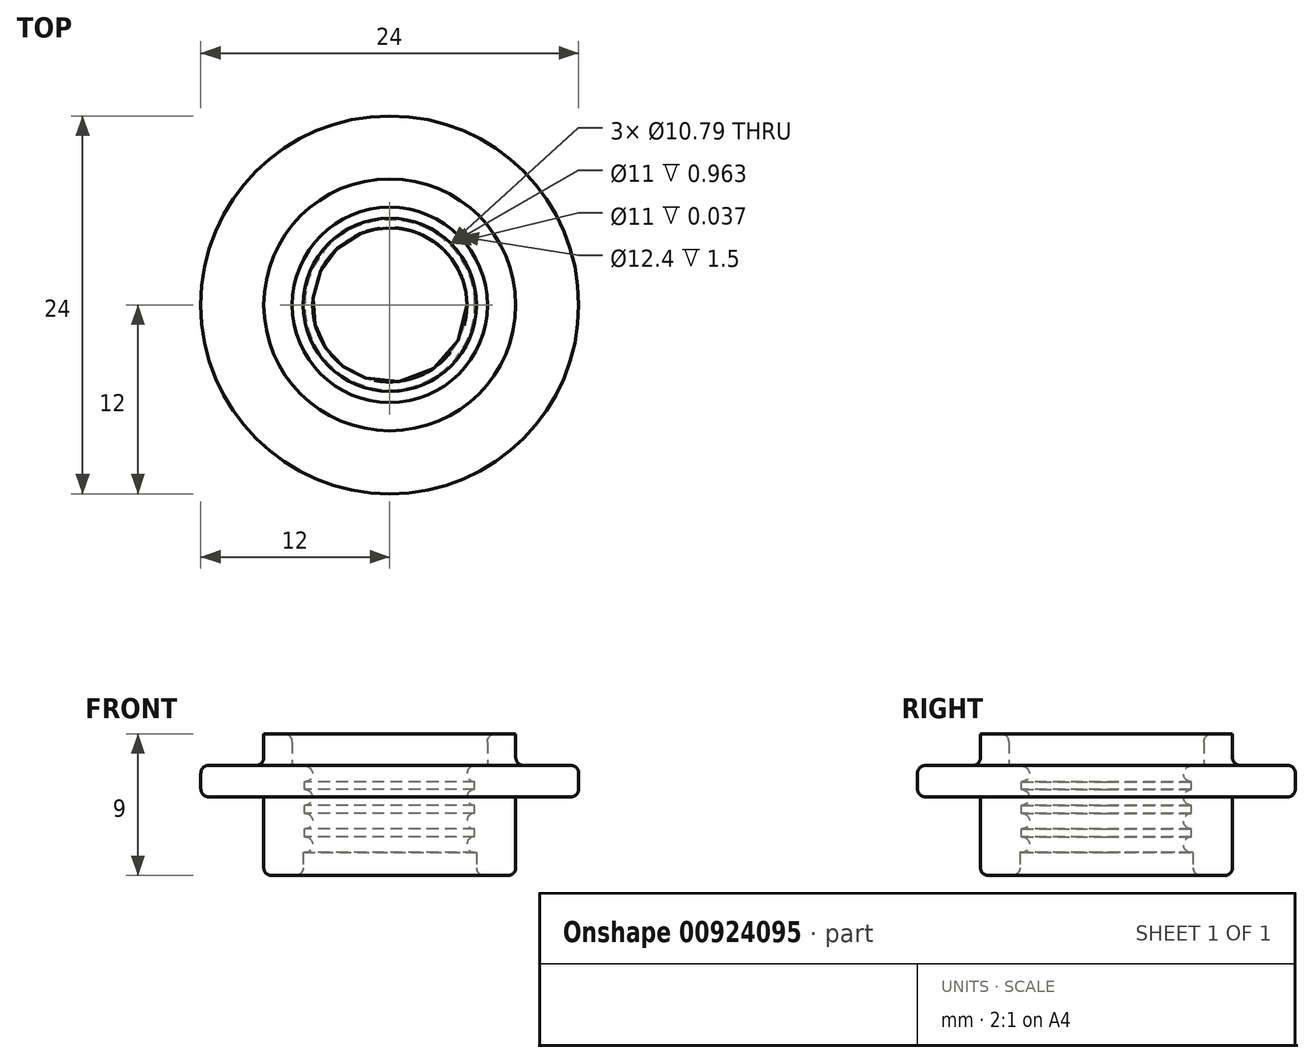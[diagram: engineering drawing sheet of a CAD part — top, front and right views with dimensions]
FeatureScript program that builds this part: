
annotation { "Feature Type Name" : "Feature", "Feature Type Description" : "" }
export const myFeature = defineFeature(function(context is Context, id is Id, definition is map)
    precondition{}
    {
        {
            var Q0;
            Q0=qCreatedBy(makeId("Front.planeOp"),FACE);
            var sketch = newSketch(context, id + "F0", { "sketchPlane" : qUnion([Q0])});
            skLineSegment(sketch, "E0", {"start": v(0, -6.66) * mm, "end": v(0, 13.65) * mm, "construction": true});
            skLineSegment(sketch, "E1", {"start": v(5.5, 0) * mm, "end": v(5.5, 7) * mm});
            skLineSegment(sketch, "E2", {"start": v(5.5, 7) * mm, "end": v(6.2, 7) * mm});
            skLineSegment(sketch, "E3", {"start": v(6.2, 7) * mm, "end": v(6.2, 9) * mm});
            skLineSegment(sketch, "E4", {"start": v(6.2, 9) * mm, "end": v(8, 9) * mm});
            skLineSegment(sketch, "E5", {"start": v(8, 9) * mm, "end": v(8, 7) * mm});
            skLineSegment(sketch, "E6", {"start": v(8, 7) * mm, "end": v(12, 7) * mm});
            skLineSegment(sketch, "E7", {"start": v(12, 7) * mm, "end": v(12, 5) * mm});
            skLineSegment(sketch, "E8", {"start": v(12, 5) * mm, "end": v(8, 5) * mm});
            skLineSegment(sketch, "E9", {"start": v(8, 5) * mm, "end": v(8, 0) * mm});
            skLineSegment(sketch, "E10", {"start": v(8, 0) * mm, "end": v(5.5, 0) * mm});
            skSolve(sketch);
        }
        {
            var Q0;
            Q0 = qSketchRegion(id + "F0", true);
            var Q1;
            Q1=sQuery(id+"F0.wireOp",EDGE,"E0");
            revolve(context, id + "F1", {"surfaceOperationType" : NewSurfaceOperationType.NEW, "entities" : qUnion([Q0]), "axis" : qUnion([Q1]), "revolveType" : RevolveType.FULL});
        }
        {
            var Q0;
            Q0=makeQuery(id+"F1.opRevolve","SWEPT_EDGE",EDGE,{"disambiguationData":[OSD([sQuery(id+"F0.wireOp",EDGE,"E5"),sQuery(id+"F0.wireOp",EDGE,"E6")])]});
            var Q1;
            Q1=makeQuery(id+"F1.opRevolve","SWEPT_EDGE",EDGE,{"disambiguationData":[OSD([sQuery(id+"F0.wireOp",EDGE,"E3"),sQuery(id+"F0.wireOp",EDGE,"E4")])]});
            var Q2;
            Q2=makeQuery(id+"F1.opRevolve","SWEPT_EDGE",EDGE,{"disambiguationData":[OSD([sQuery(id+"F0.wireOp",EDGE,"E6"),sQuery(id+"F0.wireOp",EDGE,"E7")])]});
            var Q3;
            Q3=makeQuery(id+"F1.opRevolve","SWEPT_EDGE",EDGE,{"disambiguationData":[OSD([sQuery(id+"F0.wireOp",EDGE,"E7"),sQuery(id+"F0.wireOp",EDGE,"E8")])]});
            var Q4;
            Q4=makeQuery(id+"F1.opRevolve","SWEPT_EDGE",EDGE,{"disambiguationData":[OSD([sQuery(id+"F0.wireOp",EDGE,"E9"),sQuery(id+"F0.wireOp",EDGE,"E10")])]});
            var Q5;
            Q5=makeQuery(id+"F1.opRevolve","SWEPT_EDGE",EDGE,{"disambiguationData":[OSD([sQuery(id+"F0.wireOp",EDGE,"E1"),sQuery(id+"F0.wireOp",EDGE,"E10")])]});
            fillet(context, id + "F2", {"entities" : qUnion([Q0, Q1, Q2, Q3, Q4, Q5]), "radius" : 0.5 * mm, "tangentPropagation" : true, "allowEdgeOverflow" : false});
        }
        {
            var Q0;
            Q0=qCreatedBy(makeId("Front.planeOp"),FACE);
            var sketch = newSketch(context, id + "F3", { "sketchPlane" : qUnion([Q0])});
            skArc(sketch, "E11", {"start": v(5.4, 2.46) * mm, "mid": v(4.9, 1.96) * mm, "end": v(5.4, 1.46) * mm});
            skArc(sketch, "E12.1.0.0", {"start": v(5.4, 3.96) * mm, "mid": v(4.9, 3.46) * mm, "end": v(5.4, 2.96) * mm});
            skArc(sketch, "E12.2.0.0", {"start": v(5.4, 5.46) * mm, "mid": v(4.9, 4.96) * mm, "end": v(5.4, 4.46) * mm});
            skArc(sketch, "E12.3.0.0", {"start": v(5.4, 6.96) * mm, "mid": v(4.9, 6.46) * mm, "end": v(5.4, 5.96) * mm});
            skLineSegment(sketch, "E13", {"start": v(0, 10.63) * mm, "end": v(0, -1.11) * mm, "construction": true});
            skLineSegment(sketch, "E14.trimOffspring", {"start": v(5.4, 5.96) * mm, "end": v(5.4, 5.46) * mm});
            skLineSegment(sketch, "E15.trimOffspring", {"start": v(5.4, 4.46) * mm, "end": v(5.4, 3.96) * mm});
            skLineSegment(sketch, "E16.trimOffspring", {"start": v(5.4, 2.96) * mm, "end": v(5.4, 2.46) * mm});
            skLineSegment(sketch, "E17.trimOffspring", {"start": v(5.4, 2.46) * mm, "end": v(5.4, 2.96) * mm, "construction": true});
            skLineSegment(sketch, "E18", {"start": v(5.63, 6.96) * mm, "end": v(5.63, 1.46) * mm});
            skLineSegment(sketch, "E19", {"start": v(5.63, 1.46) * mm, "end": v(5.4, 1.46) * mm});
            skLineSegment(sketch, "E20", {"start": v(5.4, 6.96) * mm, "end": v(5.63, 6.96) * mm});
            skSolve(sketch);
        }
        {
            var Q0;
            Q0=makeQuery(id+"F3.imprint","IMPRINT",FACE,{"disambiguationData":[TD([[makeQuery(id+"F3.imprint","IMPRINT",EDGE,{"derivedFrom":sQuery(id+"F3.wireOp",EDGE,"E11")}),1.0]])]});
            var Q1;
            Q1=sQuery(id+"F3.wireOp",EDGE,"E13");
            revolve(context, id + "F4", {"operationType" : NewBodyOperationType.ADD, "surfaceOperationType" : NewSurfaceOperationType.NEW, "entities" : qUnion([Q0]), "axis" : qUnion([Q1]), "revolveType" : RevolveType.FULL});
        }
    });
